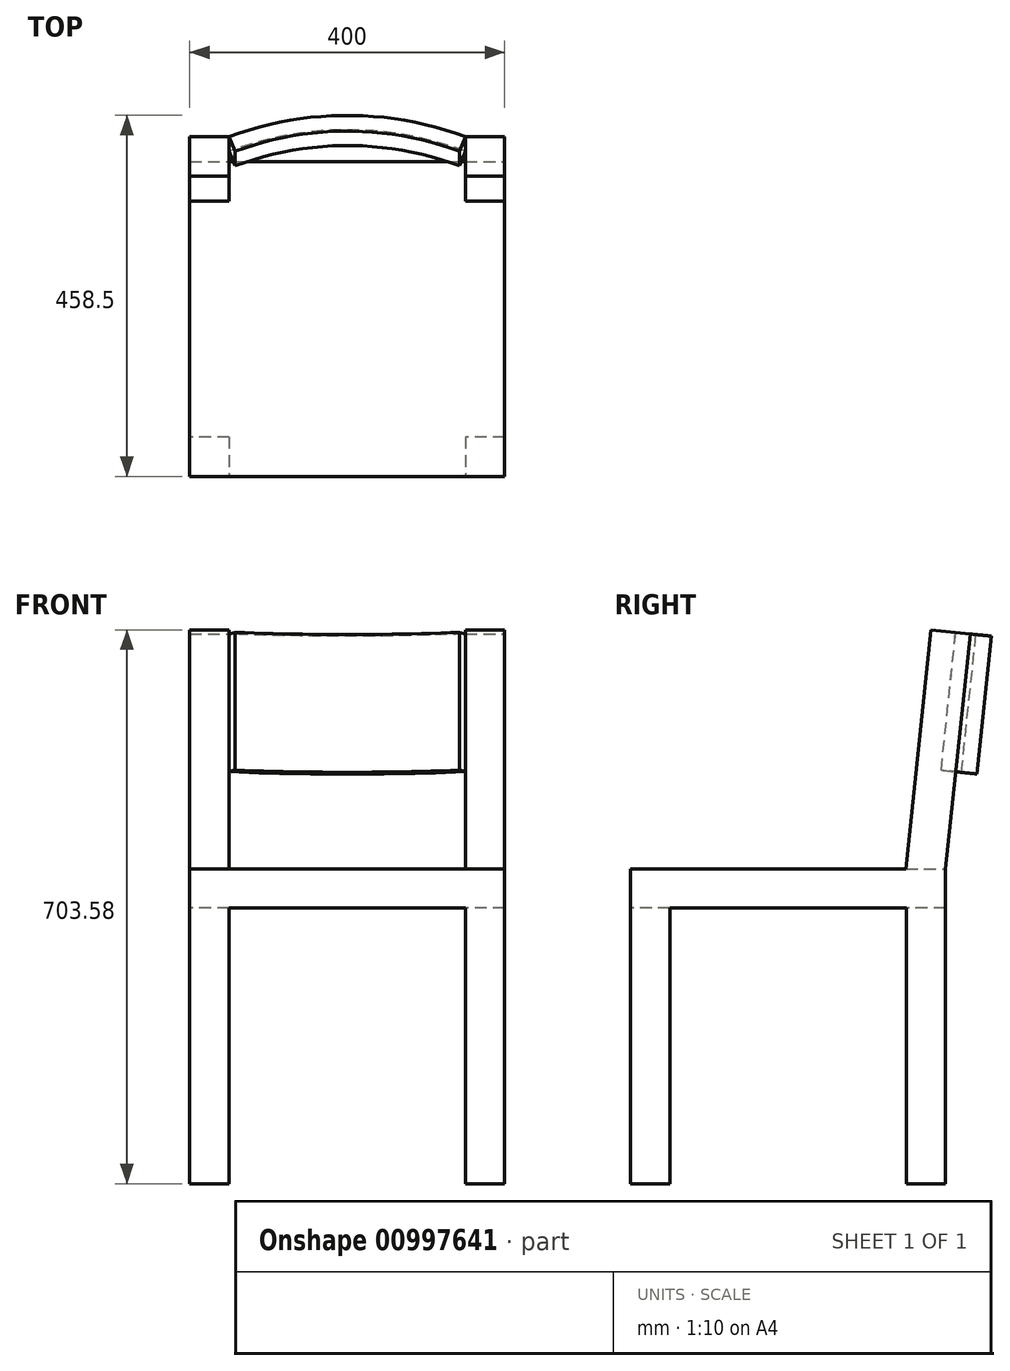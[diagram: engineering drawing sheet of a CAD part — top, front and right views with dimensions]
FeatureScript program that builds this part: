
annotation { "Feature Type Name" : "Feature", "Feature Type Description" : "" }
export const myFeature = defineFeature(function(context is Context, id is Id, definition is map)
    precondition{}
    {
        {
            var Q0;
            Q0=qCreatedBy(makeId("Top.planeOp"),FACE);
            var sketch = newSketch(context, id + "F0", { "sketchPlane" : qUnion([Q0])});
            skLineSegment(sketch, "E0.bottom", {"start": v(-200, 200) * mm, "end": v(200, 200) * mm});
            skLineSegment(sketch, "E0.top", {"start": v(-200, -200) * mm, "end": v(200, -200) * mm});
            skLineSegment(sketch, "E0.left", {"start": v(-200, 200) * mm, "end": v(-200, -200) * mm});
            skLineSegment(sketch, "E0.right", {"start": v(200, 200) * mm, "end": v(200, -200) * mm});
            skPoint(sketch, "E0.middle", {"position": v(0, 0) * mm});
            skSolve(sketch);
        }
        {
            var Q0;
            Q0=makeQuery(id+"F0.imprint","IMPRINT",FACE,{"disambiguationData":[TD([[makeQuery(id+"F0.imprint","IMPRINT",EDGE,{"derivedFrom":sQuery(id+"F0.wireOp",EDGE,"E0.bottom")}),-1.0]])]});
            extrude(context, id + "F1", {"entities" : qUnion([Q0]), "depth" : 400 * mm, "offsetDistance" : 25 * mm});
        }
        {
            var Q0;
            Q0=makeQuery(id+"F1.opExtrude","SWEPT_FACE",FACE,{"disambiguationData":[OSD([sQuery(id+"F0.wireOp",EDGE,"E0.top")])]});
            var sketch = newSketch(context, id + "F2", { "sketchPlane" : qUnion([Q0])});
            skLineSegment(sketch, "E1.bottom", {"start": v(150, 350) * mm, "end": v(-150, 350) * mm});
            skLineSegment(sketch, "E1.top", {"start": v(150, 0) * mm, "end": v(-150, 0) * mm});
            skLineSegment(sketch, "E1.left", {"start": v(150, 350) * mm, "end": v(150, 0) * mm});
            skLineSegment(sketch, "E1.right", {"start": v(-150, 350) * mm, "end": v(-150, 0) * mm});
            skPoint(sketch, "E1.middle", {"position": v(0, 175) * mm});
            skSolve(sketch);
        }
        {
            var Q0;
            Q0=makeQuery(id+"F2.imprint","IMPRINT",FACE,{"disambiguationData":[TD([[makeQuery(id+"F2.imprint","IMPRINT",EDGE,{"derivedFrom":sQuery(id+"F2.wireOp",EDGE,"E1.bottom")}),1.0]])]});
            extrude(context, id + "F3", {"entities" : qUnion([Q0]), "operationType" : NewBodyOperationType.REMOVE, "endBound" : BoundingType.THROUGH_ALL, "oppositeDirection" : true, "depth" : 25 * mm, "offsetDistance" : 25 * mm});
        }
        {
            var Q0;
            Q0=makeQuery(id+"F1.opExtrude","SWEPT_FACE",FACE,{"disambiguationData":[OSD([sQuery(id+"F0.wireOp",EDGE,"E0.left")])]});
            var sketch = newSketch(context, id + "F4", { "sketchPlane" : qUnion([Q0])});
            skLineSegment(sketch, "E2.bottom", {"start": v(-150, 0) * mm, "end": v(150, 0) * mm});
            skLineSegment(sketch, "E2.top", {"start": v(-150, 350) * mm, "end": v(150, 350) * mm});
            skLineSegment(sketch, "E2.left", {"start": v(-150, 0) * mm, "end": v(-150, 350) * mm});
            skLineSegment(sketch, "E2.right", {"start": v(150, 0) * mm, "end": v(150, 350) * mm});
            skPoint(sketch, "E2.middle", {"position": v(0, 175) * mm});
            skSolve(sketch);
        }
        {
            var Q0;
            Q0=makeQuery(id+"F4.imprint","IMPRINT",FACE,{"disambiguationData":[TD([[makeQuery(id+"F4.imprint","IMPRINT",EDGE,{"derivedFrom":sQuery(id+"F4.wireOp",EDGE,"E2.bottom")}),1.0]])]});
            extrude(context, id + "F5", {"entities" : qUnion([Q0]), "operationType" : NewBodyOperationType.REMOVE, "endBound" : BoundingType.THROUGH_ALL, "oppositeDirection" : true, "depth" : 25 * mm, "offsetDistance" : 25 * mm});
        }
        {
            var Q0;
            Q0=makeQuery(id+"F1.opExtrude","CAP_FACE",FACE,{"disambiguationData":[OSD([sQuery(id+"F0.wireOp",EDGE,"E0.bottom"),sQuery(id+"F0.wireOp",EDGE,"E0.top"),sQuery(id+"F0.wireOp",EDGE,"E0.left"),sQuery(id+"F0.wireOp",EDGE,"E0.right")])],"isStart":false});
            cPlane(context, id + "F6", {"entities" : qUnion([Q0]), "cplaneType" : CPlaneType.OFFSET, "offset" : 25 * mm, "width" : 150 * mm, "height" : 150 * mm});
        }
        {
            var Q0;
            Q0=makeQuery(id+"F1.opExtrude","CAP_FACE",FACE,{"disambiguationData":[OSD([sQuery(id+"F0.wireOp",EDGE,"E0.bottom"),sQuery(id+"F0.wireOp",EDGE,"E0.top"),sQuery(id+"F0.wireOp",EDGE,"E0.left"),sQuery(id+"F0.wireOp",EDGE,"E0.right")])],"isStart":false});
            var sketch = newSketch(context, id + "F7", { "sketchPlane" : qUnion([Q0])});
            skLineSegment(sketch, "E3", {"start": v(-200, 200) * mm, "end": v(200, 200) * mm});
            skSolve(sketch);
        }
        {
            var Q0;
            Q0=sQuery(id+"F7.wireOp",EDGE,"E3");
            cPlane(context, id + "F8", {"entities" : qUnion([Q0]), "cplaneType" : CPlaneType.LINE_ANGLE, "offset" : 25 * mm, "angle" : 6 * degree, "oppositeDirection" : true, "width" : 150 * mm, "height" : 150 * mm});
        }
        {
            var Q0;
            Q0=qCreatedBy(id+"F8.planeOp",FACE);
            var sketch = newSketch(context, id + "F9", { "sketchPlane" : qUnion([Q0])});
            skLineSegment(sketch, "E4.bottom", {"start": v(200, 718.71) * mm, "end": v(-200, 718.71) * mm});
            skLineSegment(sketch, "E4.top", {"start": v(200, 418.71) * mm, "end": v(-200, 418.71) * mm});
            skLineSegment(sketch, "E4.left", {"start": v(200, 718.71) * mm, "end": v(200, 418.71) * mm});
            skLineSegment(sketch, "E4.right", {"start": v(-200, 718.71) * mm, "end": v(-200, 418.71) * mm});
            skSolve(sketch);
        }
        {
            var Q0;
            Q0=makeQuery(id+"F9.imprint","IMPRINT",FACE,{"disambiguationData":[TD([[makeQuery(id+"F9.imprint","IMPRINT",EDGE,{"derivedFrom":sQuery(id+"F9.wireOp",EDGE,"E4.bottom")}),1.0]])]});
            extrude(context, id + "F10", {"entities" : qUnion([Q0]), "oppositeDirection" : true, "depth" : 50 * mm, "offsetDistance" : 25 * mm});
        }
        {
            var Q0;
            Q0=makeQuery(id+"F10.opExtrude","CAP_FACE",FACE,{"disambiguationData":[OSD([sQuery(id+"F9.wireOp",EDGE,"E4.bottom"),sQuery(id+"F9.wireOp",EDGE,"E4.top"),sQuery(id+"F9.wireOp",EDGE,"E4.left"),sQuery(id+"F9.wireOp",EDGE,"E4.right")])],"isStart":false});
            var sketch = newSketch(context, id + "F11", { "sketchPlane" : qUnion([Q0])});
            skLineSegment(sketch, "E5.bottom", {"start": v(-150, 718.71) * mm, "end": v(150, 718.71) * mm});
            skLineSegment(sketch, "E5.top", {"start": v(-150, 418.71) * mm, "end": v(150, 418.71) * mm});
            skLineSegment(sketch, "E5.left", {"start": v(-150, 718.71) * mm, "end": v(-150, 418.71) * mm});
            skLineSegment(sketch, "E5.right", {"start": v(150, 718.71) * mm, "end": v(150, 418.71) * mm});
            skPoint(sketch, "E5.middle", {"position": v(0, 568.71) * mm});
            skPoint(sketch, "E6.middle", {"position": v(-150, 418.71) * mm});
            skSolve(sketch);
        }
        {
            var Q0;
            Q0 = qSketchRegion(id + "F11", true);
            extrude(context, id + "F12", {"entities" : qUnion([Q0]), "operationType" : NewBodyOperationType.REMOVE, "oppositeDirection" : true, "depth" : 50 * mm, "offsetDistance" : 25 * mm});
        }
        {
            var Q0;
            {var subQ0=sQuery(id+"F9.wireOp",EDGE,"E4.right");var subQ3=sQuery(id+"F9.wireOp",EDGE,"E4.bottom");Q0=makeQuery(id+"F12.boolean.opBoolean","SPLIT",FACE,{"disambiguationData":[TD([makeQuery(id+"F10.opExtrude","SWEPT_FACE",FACE,{"disambiguationData":[OSD([subQ0])]})])],"derivedFrom":makeQuery(id+"F10.opExtrude","SWEPT_FACE",FACE,{"disambiguationData":[OSD([subQ3])]})});}
            var Q1;
            {var subQ1=sQuery(id+"F9.wireOp",EDGE,"E4.left");var subQ3=sQuery(id+"F9.wireOp",EDGE,"E4.bottom");Q1=makeQuery(id+"F12.boolean.opBoolean","SPLIT",FACE,{"disambiguationData":[TD([makeQuery(id+"F10.opExtrude","SWEPT_FACE",FACE,{"disambiguationData":[OSD([subQ1])]})])],"derivedFrom":makeQuery(id+"F10.opExtrude","SWEPT_FACE",FACE,{"disambiguationData":[OSD([subQ3])]})});}
            cPlane(context, id + "F13", {"entities" : qUnion([Q0, Q1]), "cplaneType" : CPlaneType.MID_PLANE, "offset" : 25 * mm, "width" : 150 * mm, "height" : 150 * mm});
        }
        {
            var Q0;
            {var subQ0=sQuery(id+"F9.wireOp",EDGE,"E4.right");var subQ2=sQuery(id+"F9.wireOp",EDGE,"E4.top");Q0=makeQuery(id+"F12.boolean.opBoolean","SPLIT",FACE,{"disambiguationData":[TD([makeQuery(id+"F10.opExtrude","SWEPT_FACE",FACE,{"disambiguationData":[OSD([subQ0])]})])],"derivedFrom":makeQuery(id+"F10.opExtrude","SWEPT_FACE",FACE,{"disambiguationData":[OSD([subQ2])]})});}
            extrude(context, id + "F14", {"entities" : qUnion([Q0]), "operationType" : NewBodyOperationType.ADD, "endBound" : BoundingType.UP_TO_NEXT, "depth" : 25 * mm, "offsetDistance" : 25 * mm});
        }
        {
            var Q0;
            {var subQ1=sQuery(id+"F9.wireOp",EDGE,"E4.left");var subQ2=sQuery(id+"F9.wireOp",EDGE,"E4.top");Q0=makeQuery(id+"F12.boolean.opBoolean","SPLIT",FACE,{"disambiguationData":[TD([makeQuery(id+"F10.opExtrude","SWEPT_FACE",FACE,{"disambiguationData":[OSD([subQ1])]})])],"derivedFrom":makeQuery(id+"F10.opExtrude","SWEPT_FACE",FACE,{"disambiguationData":[OSD([subQ2])]})});}
            extrude(context, id + "F15", {"entities" : qUnion([Q0]), "operationType" : NewBodyOperationType.ADD, "endBound" : BoundingType.UP_TO_NEXT, "depth" : 25 * mm, "offsetDistance" : 25 * mm});
        }
        {
            var Q0;
            Q0=qCreatedBy(id+"F13.planeOp",FACE);
            var sketch = newSketch(context, id + "F16", { "sketchPlane" : qUnion([Q0])});
            skArc(sketch, "E7", {"start": v(150, 157.1) * mm, "mid": v(0, 184.39) * mm, "end": v(-150, 157.1) * mm});
            skArc(sketch, "E8.0", {"start": v(142.77, 138.45) * mm, "mid": v(0.06, 164.39) * mm, "end": v(-142.65, 138.49) * mm});
            skLineSegment(sketch, "E9", {"start": v(-142.65, 138.49) * mm, "end": v(-150, 157.1) * mm});
            skLineSegment(sketch, "E10", {"start": v(142.77, 138.45) * mm, "end": v(150, 157.1) * mm});
            skSolve(sketch);
        }
        {
            var Q0;
            Q0=makeQuery(id+"F16.imprint","IMPRINT",FACE,{"disambiguationData":[TD([[makeQuery(id+"F16.imprint","IMPRINT",EDGE,{"derivedFrom":sQuery(id+"F16.wireOp",EDGE,"E7")}),1.0]])]});
            extrude(context, id + "F17", {"entities" : qUnion([Q0]), "oppositeDirection" : true, "depth" : 176 * mm, "offsetDistance" : 25 * mm});
        }
    });
